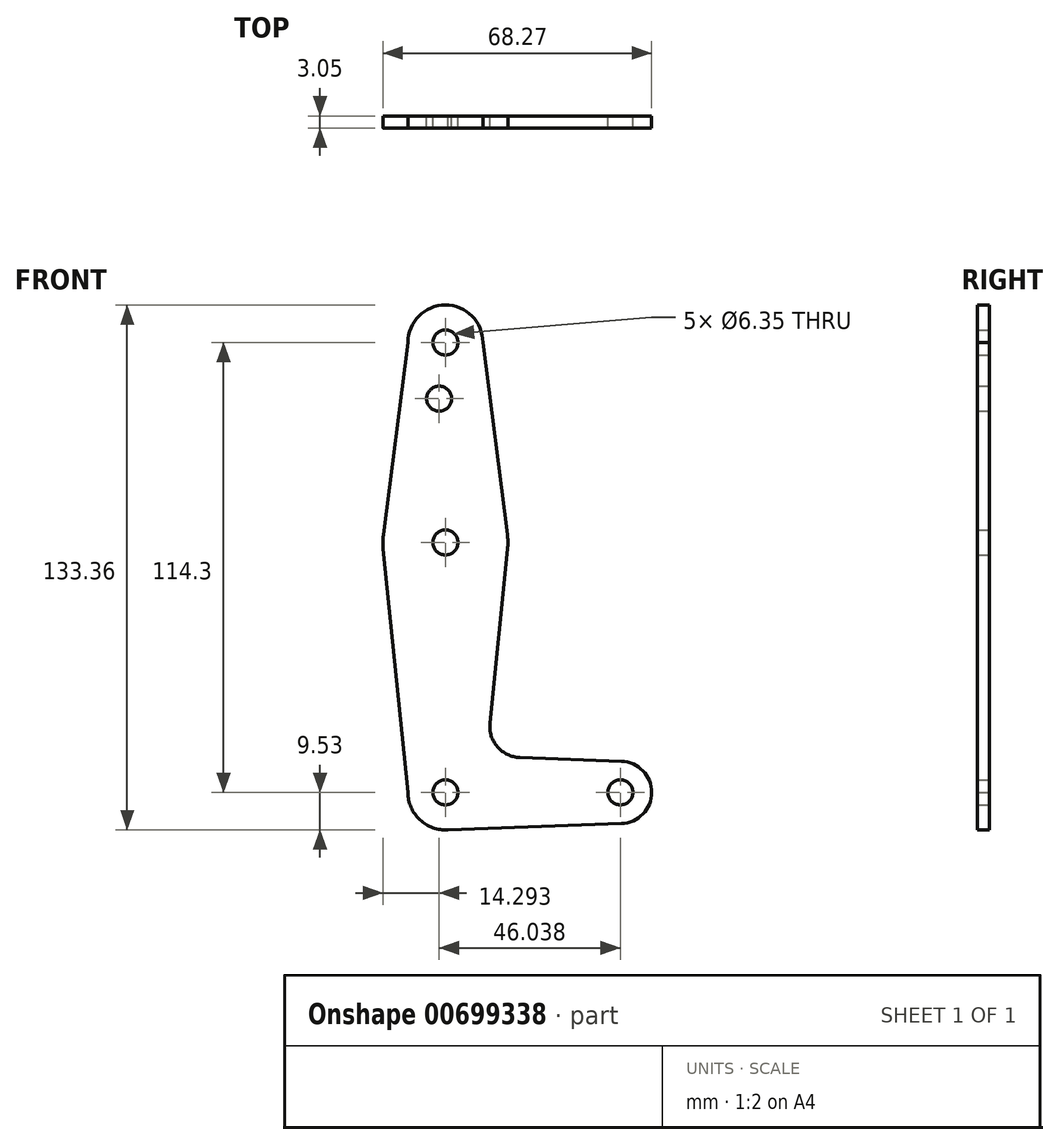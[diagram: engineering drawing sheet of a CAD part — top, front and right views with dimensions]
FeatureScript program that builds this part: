
annotation { "Feature Type Name" : "Feature", "Feature Type Description" : "" }
export const myFeature = defineFeature(function(context is Context, id is Id, definition is map)
    precondition{}
    {
        {
            var Q0;
            Q0=qCreatedBy(makeId("Front.planeOp"),FACE);
            var sketch = newSketch(context, id + "F0", { "sketchPlane" : qUnion([Q0])});
            skLineSegment(sketch, "E0", {"start": v(0, 114.3) * mm, "end": v(0, 0) * mm, "construction": true});
            skLineSegment(sketch, "E1", {"start": v(0, 0) * mm, "end": v(44.45, 0) * mm, "construction": true});
            skCircle(sketch, "E2", {"center": v(0, 114.3) * mm, "radius": 9.53 * mm});
            skCircle(sketch, "E3", {"center": v(0, 63.5) * mm, "radius": 15.88 * mm});
            skCircle(sketch, "E4", {"center": v(0, 0) * mm, "radius": 9.53 * mm});
            skCircle(sketch, "E5", {"center": v(44.45, 0) * mm, "radius": 7.94 * mm});
            skLineSegment(sketch, "E6", {"start": v(18.93, 8.85) * mm, "end": v(44.73, 7.93) * mm});
            skLineSegment(sketch, "E7", {"start": v(0, -9.53) * mm, "end": v(44.73, -7.93) * mm});
            skLineSegment(sketch, "E8", {"start": v(9.52, 114.3) * mm, "end": v(15.75, 65.5) * mm});
            skLineSegment(sketch, "E9", {"start": v(-9.53, 114.3) * mm, "end": v(-15.75, 65.5) * mm});
            skLineSegment(sketch, "E10", {"start": v(11.3, 17.6) * mm, "end": v(15.8, 61.9) * mm});
            skLineSegment(sketch, "E11", {"start": v(-9.53, 0) * mm, "end": v(-15.8, 61.9) * mm});
            skArc(sketch, "E12.filletArc", {"start": v(11.3, 17.6) * mm, "mid": v(13.22, 11.57) * mm, "end": v(18.93, 8.85) * mm});
            skCircle(sketch, "E13", {"center": v(0, 114.3) * mm, "radius": 3.18 * mm});
            skCircle(sketch, "E14", {"center": v(0, 63.5) * mm, "radius": 3.18 * mm});
            skCircle(sketch, "E15", {"center": v(0, 0) * mm, "radius": 3.18 * mm});
            skCircle(sketch, "E16", {"center": v(44.45, 0) * mm, "radius": 3.18 * mm});
            skCircle(sketch, "E17", {"center": v(-1.59, 100.03) * mm, "radius": 3.18 * mm});
            skSolve(sketch);
        }
        {
            var Q0;
            Q0 = qSketchRegion(id + "F0", true);
            extrude(context, id + "F1", {"entities" : qUnion([Q0]), "depth" : 3.05 * mm, "offsetDistance" : 25.4 * mm});
        }
    });
